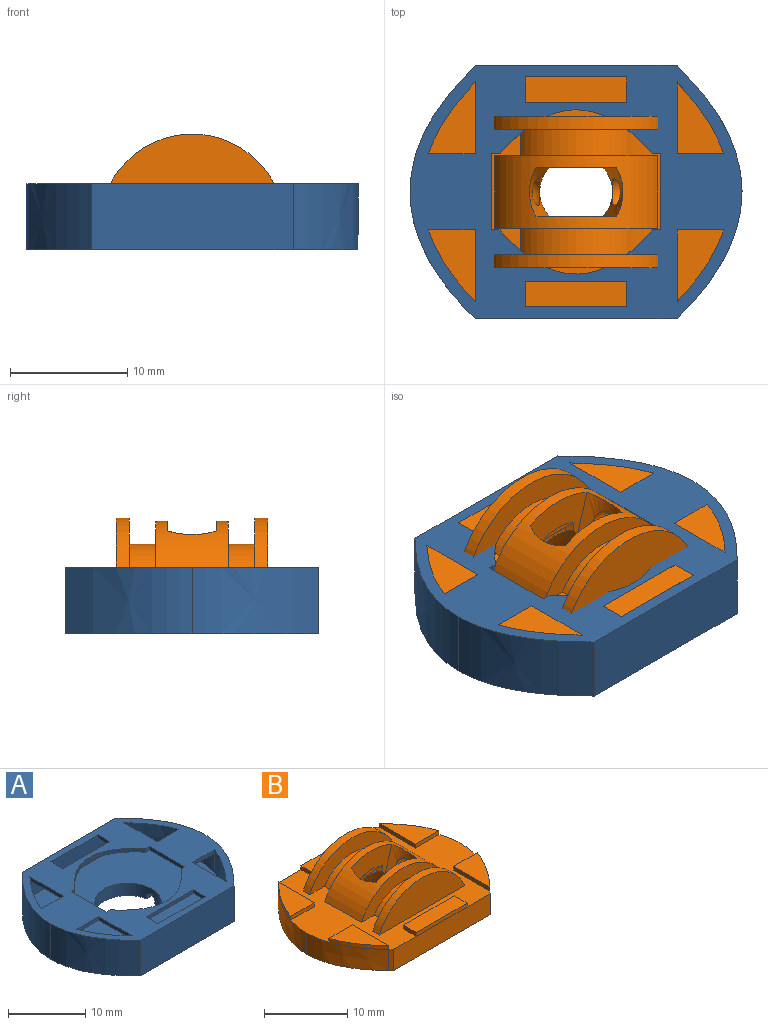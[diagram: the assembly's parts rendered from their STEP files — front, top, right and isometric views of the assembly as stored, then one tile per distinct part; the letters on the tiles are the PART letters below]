
ASSEMBLY  parts=2 mates=1
PART A: 58 faces, bbox 28.3x21.6x5.6 mm
  f0: extruded ~3.24x3.1mm, area 10.2mm2, adj f1,f19,f24,f57
  f1: extruded ~3.24x3.1mm, area 10.2mm2, adj f0,f19,f21,f57
  f2: extruded ~3.1x0.43mm, area 1.8mm2, adj f3,f19,f21,f57
  f3: plane 16.38x3.67mm, normal (0,-1,0), area 55.7mm2, adj f2,f4,f19,f48,f50,f56,f57
  f4: extruded ~3.1x0.43mm, area 1.9mm2, adj f3,f19,f22,f57
  f5: extruded ~3.1x2.45mm, area 7.8mm2, adj f6,f19,f22,f57
  f6: extruded ~3.1x1.41mm, area 4.4mm2, adj f5,f7,f19,f57
  f7: extruded ~3.1x2.62mm, area 8.3mm2, adj f6,f19,f23,f57
  f8: extruded ~3.1x0.43mm, area 1.9mm2, adj f9,f19,f23,f57
  f9: plane 16.38x3.67mm, normal (0,1,0), area 55.7mm2, adj f8,f10,f19,f30,f51,f56,f57
  f10: extruded ~3.1x0.43mm, area 1.8mm2, adj f9,f19,f24,f57
  f11: cylinder r=4.31mm len=8.63mm, axis (0,0,-1), area 52.2mm2, adj f19,f20,f25,f26,f27,f28
  f12: extruded ~10.82x5.64mm, area 70.5mm2, adj f13,f18,f20,f56
  f13: plane 17.21x5.64mm, normal (0,-1,0), area 97.1mm2, adj f12,f14,f20,f56
  f14: extruded ~10.2x5.64mm, area 66.9mm2, adj f13,f15,f20,f26,f56
  f15: extruded ~5.08x1.41mm, area 6.7mm2, adj f14,f16,f27,f28,f56
  f16: extruded ~10.03x5.64mm, area 66mm2, adj f15,f17,f20,f25,f56
  f17: plane 17.21x5.64mm, normal (0,1,0), area 97.1mm2, adj f16,f18,f20,f56
  f18: extruded ~10.82x5.64mm, area 70.5mm2, adj f12,f17,f20,f56
  f19: plane 26.28x19.62mm, normal (0,0,1), area 391.9mm2, adj f0,f1,f2,f3,f4,f5,f6,f7
  f20: plane 28.29x21.65mm, normal (0,0,-1), area 460.4mm2, adj f11,f12,f13,f14,f16,f17,f18,f25
  f21: extruded ~6.14x4mm, area 27.1mm2, adj f1,f2,f19,f29,f55,f56
  f22: extruded ~6.14x3.97mm, area 27mm2, adj f4,f5,f19,f46,f47,f56
  f23: extruded ~6.14x3.97mm, area 27mm2, adj f7,f8,f19,f32,f52,f56
  f24: extruded ~6.14x4mm, area 27.1mm2, adj f0,f10,f19,f33,f53,f56
  f25: plane 9.87x0.56mm, normal (0,-1,0), area 5.6mm2, adj f11,f16,f20,f28
  f26: plane 9.86x0.56mm, normal (0,1,0), area 5.6mm2, adj f11,f14,f20,f27
  f27: plane 9.88x0.71mm, normal (0,0.71,-0.71), area 9.8mm2, adj f11,f15,f26,f28
  f28: plane 9.9x0.71mm, normal (0,-0.71,-0.71), area 9.8mm2, adj f11,f15,f25,f27
  f29: plane 4x0.56mm, normal (0,1,0), area 2.3mm2, adj f21,f55,f56,f57
  f30: plane 2.18x0.56mm, normal (1,0,0), area 1.2mm2, adj f9,f31,f56,f57
  f31: plane 8.63x0.56mm, normal (0,-1,0), area 4.9mm2, adj f30,f51,f56,f57
  f32: plane 6.14x0.56mm, normal (1,0,0), area 3.5mm2, adj f23,f52,f56,f57
  f33: plane 6.14x0.56mm, normal (-1,0,0), area 3.5mm2, adj f24,f53,f56,f57
  f34: extruded ~4.31x1.66mm, area 2.7mm2, adj f35,f54,f56,f57
  f35: extruded ~2.18x2.1mm, area 1.7mm2, adj f34,f36,f56,f57
  f36: plane 0.71x0.56mm, normal (0,-1,0), area 0.4mm2, adj f35,f37,f56,f57
  f37: plane 6.48x0.56mm, normal (-1,0,0), area 3.7mm2, adj f36,f38,f56,f57
  f38: plane 0.71x0.56mm, normal (0,1,0), area 0.4mm2, adj f37,f39,f56,f57
  f39: extruded ~2.18x2.1mm, area 1.7mm2, adj f38,f40,f56,f57
  f40: extruded ~8.63x1.66mm, area 5.3mm2, adj f39,f41,f56,f57
  f41: extruded ~2.18x2.1mm, area 1.7mm2, adj f40,f42,f56,f57
  f42: plane 0.71x0.56mm, normal (0,1,0), area 0.4mm2, adj f41,f43,f56,f57
  f43: plane 6.48x0.56mm, normal (1,0,0), area 3.7mm2, adj f42,f44,f56,f57
  f44: plane 0.71x0.56mm, normal (0,-1,0), area 0.4mm2, adj f43,f45,f56,f57
  f45: extruded ~2.18x2.1mm, area 1.7mm2, adj f44,f54,f56,f57
  f46: plane 3.97x0.56mm, normal (0,1,0), area 2.2mm2, adj f22,f47,f56,f57
  f47: plane 6.14x0.56mm, normal (1,0,0), area 3.5mm2, adj f22,f46,f56,f57
  f48: plane 2.18x0.56mm, normal (-1,0,0), area 1.2mm2, adj f3,f49,f56,f57
  f49: plane 8.63x0.56mm, normal (0,1,0), area 4.9mm2, adj f48,f50,f56,f57
  f50: plane 2.18x0.56mm, normal (1,0,0), area 1.2mm2, adj f3,f49,f56,f57
  f51: plane 2.18x0.56mm, normal (-1,0,0), area 1.2mm2, adj f9,f31,f56,f57
  f52: plane 3.97x0.56mm, normal (0,-1,0), area 2.2mm2, adj f23,f32,f56,f57
  f53: plane 4x0.56mm, normal (0,-1,0), area 2.3mm2, adj f24,f33,f56,f57
  f54: extruded ~4.31x1.66mm, area 2.7mm2, adj f34,f45,f56,f57
  f55: plane 6.14x0.56mm, normal (-1,0,0), area 3.5mm2, adj f21,f29,f56,f57
  f56: plane 28.32x21.65mm, normal (0,0,1), area 280mm2, adj f3,f9,f12,f13,f14,f15,f16,f17
  f57: plane 26.28x19.62mm, normal (0,0,-1), area 197.6mm2, adj f0,f1,f2,f3,f4,f5,f6,f7
PART B: 66 faces, bbox 26.8x20.1x9.1 mm
  f0: bspline ~6.91x4.23mm, area 13.3mm2, adj f1,f2,f11,f64,f65
  f1: sphere r=1.55mm, area 24mm2, adj f0
  f2: bspline ~7.35x4.64mm, area 18.7mm2, adj f0,f3,f7,f8,f10,f11,f65
  f3: plane 3.75x0.4mm, normal (0,-1,0), area 0.9mm2, adj f2,f4
  f4: plane 3.77x0.46mm, normal (0,-0.71,-0.71), area 1.9mm2, adj f3,f5,f7,f10
  f5: plane 3.2x1.04mm, normal (0,-1,0), area 0.9mm2, adj f4,f6,f7,f10,f11
  f6: sphere r=4.55mm, area 0mm2, adj f5,f11
  f7: cylinder r=2.82mm len=0.82mm, axis (0,0,-1), area 0.5mm2, adj f2,f4,f5,f11
  f8: bspline ~6.91x4.23mm, area 13.1mm2, adj f2,f9,f11,f64,f65
  f9: sphere r=1.55mm, area 6.3mm2, adj f8
  f10: cylinder r=2.82mm len=0.82mm, axis (0,0,-1), area 0.5mm2, adj f2,f4,f5,f11
  f11: cone r=4.23mm half-angle=21deg, axis (0,0,-1), area 79.5mm2, adj f0,f2,f5,f6,f7,f8,f10,f12
  f12: plane 26.28x19.62mm, normal (0,0,-1), area 394.2mm2, adj f11,f13,f51,f52,f53,f54,f55,f56
  f13: extruded ~9.38x4.52mm, area 33.1mm2, adj f12,f14,f50,f51,f59
  f14: plane 26.29x19.62mm, normal (0,0,1), area 194.8mm2, adj f13,f15,f18,f21,f22,f25,f26,f29
  f15: plane 2.18x0.56mm, normal (-1,0,0), area 1.2mm2, adj f14,f16,f17,f39
  f16: plane 8.63x2.18mm, normal (0,0,1), area 18.8mm2, adj f15,f17,f38,f39
  f17: plane 8.63x0.57mm, normal (0,-1,0), area 4.9mm2, adj f15,f16,f38,f57
  f18: plane 6.14x0.56mm, normal (1,0,0), area 3.5mm2, adj f14,f19,f20,f21
  f19: extruded ~6.14x4mm, area 4.2mm2, adj f18,f20,f21,f55
  f20: plane 6.14x4mm, normal (0,0,1), area 14.2mm2, adj f18,f19,f21
  f21: plane 4x0.56mm, normal (0,1,0), area 2.3mm2, adj f14,f18,f19,f20
  f22: plane 4x0.56mm, normal (0,-1,0), area 2.3mm2, adj f14,f23,f24,f25
  f23: extruded ~6.14x4mm, area 4.2mm2, adj f22,f24,f25,f54
  f24: plane 6.14x4mm, normal (0,0,1), area 14.2mm2, adj f22,f23,f25
  f25: plane 6.14x0.56mm, normal (1,0,0), area 3.5mm2, adj f14,f22,f23,f24
  f26: plane 2.18x0.56mm, normal (-1,0,0), area 1.2mm2, adj f14,f27,f28,f29
  f27: plane 8.63x0.57mm, normal (0,1,0), area 4.9mm2, adj f26,f28,f30,f52
  f28: plane 8.63x2.18mm, normal (0,0,1), area 18.8mm2, adj f26,f27,f29,f30
  f29: plane 8.63x0.56mm, normal (0,-1,0), area 4.9mm2, adj f14,f26,f28,f30
  f30: plane 2.18x0.56mm, normal (1,0,0), area 1.2mm2, adj f14,f27,f28,f29
  f31: plane 6.14x0.56mm, normal (-1,0,0), area 3.5mm2, adj f14,f32,f33,f50
  f32: plane 6.14x3.97mm, normal (0,0,1), area 14.1mm2, adj f31,f33,f50
  f33: plane 3.97x0.56mm, normal (0,-1,0), area 2.2mm2, adj f14,f31,f32,f50
  f34: plane 3.97x0.56mm, normal (0,1,0), area 2.2mm2, adj f14,f35,f36,f37
  f35: extruded ~6.14x3.97mm, area 4.2mm2, adj f34,f36,f37,f59
  f36: plane 6.14x3.97mm, normal (0,0,1), area 14.1mm2, adj f34,f35,f37
  f37: plane 6.14x0.56mm, normal (-1,0,0), area 3.5mm2, adj f14,f34,f35,f36
  f38: plane 2.18x0.56mm, normal (1,0,0), area 1.2mm2, adj f14,f16,f17,f39
  f39: plane 8.63x0.56mm, normal (0,1,0), area 4.9mm2, adj f14,f15,f16,f38
  f40: plane 14.52x4.79mm, normal (0,-1,0), area 50.2mm2, adj f14,f41
  f41: cylinder r=7.89mm len=14.52mm, axis (0,-1,0), area 20.5mm2, adj f14,f40,f42
  f42: plane 14.52x4.79mm, normal (0,1,0), area 33mm2, adj f14,f41,f49
  f43: plane 14.52x4.79mm, normal (0,1,0), area 50.2mm2, adj f14,f44
  f44: cylinder r=7.89mm len=14.52mm, axis (0,-1,0), area 20.5mm2, adj f14,f43,f45
  f45: plane 14.52x4.79mm, normal (0,-1,0), area 33mm2, adj f14,f44,f46
  f46: cylinder r=5.67mm len=9.5mm, axis (0,-1,0), area 25.4mm2, adj f14,f45,f47
  f47: plane 13.9x4.51mm, normal (0,1,0), area 27.9mm2, adj f14,f46,f65
  f48: plane 13.9x4.51mm, normal (0,-1,0), area 27.9mm2, adj f14,f49,f65
  f49: cylinder r=5.67mm len=9.5mm, axis (0,-1,0), area 25.3mm2, adj f14,f42,f48
  f50: extruded ~6.14x3.97mm, area 4.2mm2, adj f13,f31,f32,f33
  f51: extruded ~3.1x0.43mm, area 1.9mm2, adj f12,f13,f14,f52
  f52: plane 16.38x3.1mm, normal (0,1,0), area 50.8mm2, adj f12,f14,f27,f51,f53
  f53: extruded ~3.1x0.43mm, area 1.8mm2, adj f12,f14,f52,f54
  f54: extruded ~9.38x4.55mm, area 33.1mm2, adj f12,f14,f23,f53,f55
  f55: extruded ~9.38x4.55mm, area 33.1mm2, adj f12,f14,f19,f54,f56
  f56: extruded ~3.1x0.43mm, area 1.8mm2, adj f12,f14,f55,f57
  f57: plane 16.38x3.1mm, normal (0,-1,0), area 50.8mm2, adj f12,f14,f17,f56,f58
  f58: extruded ~3.1x0.43mm, area 1.9mm2, adj f12,f14,f57,f59
  f59: extruded ~9.38x4.52mm, area 33.1mm2, adj f12,f13,f14,f35,f58
  f60: cylinder r=2.82mm len=3.73mm, axis (0,0,-1), area 1.4mm2, adj f11,f61,f62,f64
  f61: plane 0.8x0.03mm, normal (0,0,-1), area 0mm2, adj f60,f62
  f62: plane 3.73x0.68mm, normal (0,0.71,-0.71), area 2.5mm2, adj f60,f61,f63,f64
  f63: plane 3.73x0.38mm, normal (0,1,0), area 0.9mm2, adj f62,f64
  f64: plane 6.87x4.66mm, normal (0,1,0), area 18.7mm2, adj f0,f8,f11,f60,f62,f63,f65
  f65: cylinder r=7.61mm len=13.9mm, axis (0,-1,0), area 75mm2, adj f0,f2,f8,f14,f47,f48,f64
PLACE A at identity
PLACE B t=(0,0,1.97)mm
MATE planar B.f20 <-> A.f56  axis (0,0,1) through (-8.61,-9.38,5.64)mm
